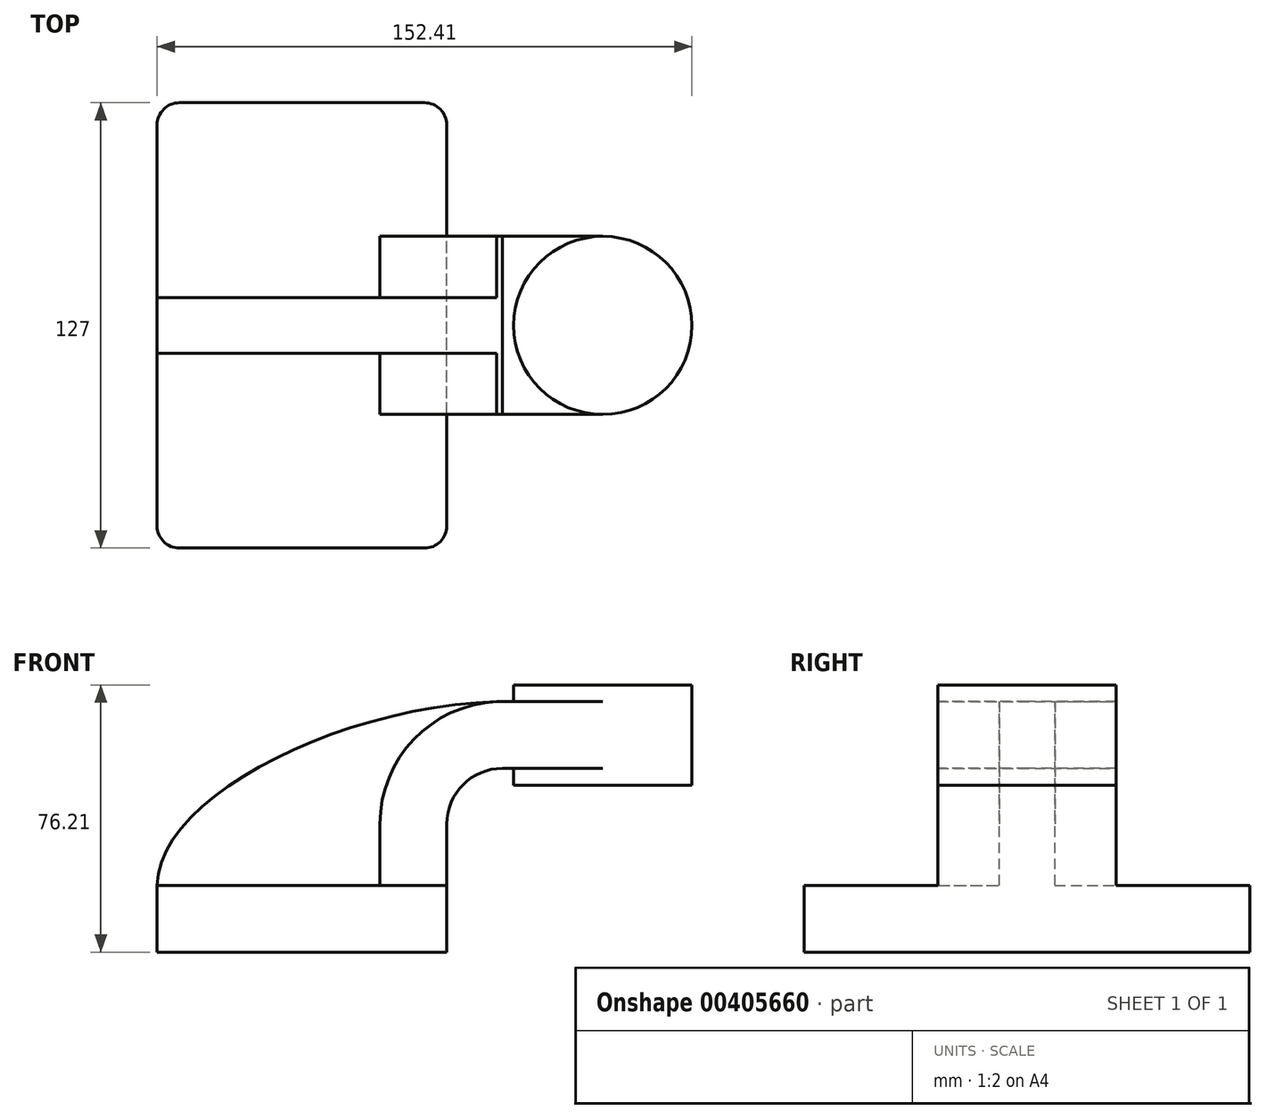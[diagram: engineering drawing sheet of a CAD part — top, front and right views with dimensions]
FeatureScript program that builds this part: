
annotation { "Feature Type Name" : "Feature", "Feature Type Description" : "" }
export const myFeature = defineFeature(function(context is Context, id is Id, definition is map)
    precondition{}
    {
        {
            var Q0;
            Q0=qCreatedBy(makeId("Front.planeOp"),FACE);
            var sketch = newSketch(context, id + "F0", { "sketchPlane" : qUnion([Q0])});
            skLineSegment(sketch, "E0.bottom", {"start": v(-41.28, -9.52) * mm, "end": v(41.28, -9.52) * mm});
            skLineSegment(sketch, "E0.top", {"start": v(-41.28, 9.52) * mm, "end": v(41.27, 9.52) * mm});
            skLineSegment(sketch, "E0.left", {"start": v(-41.27, -9.52) * mm, "end": v(-41.28, 9.52) * mm});
            skLineSegment(sketch, "E0.right", {"start": v(41.28, -9.52) * mm, "end": v(41.27, 9.52) * mm});
            skPoint(sketch, "E0.middle", {"position": v(0, 0) * mm});
            skLineSegment(sketch, "E1.bottom", {"start": v(60.32, 38.1) * mm, "end": v(111.12, 38.1) * mm});
            skLineSegment(sketch, "E1.top", {"start": v(60.32, 66.68) * mm, "end": v(111.12, 66.68) * mm});
            skLineSegment(sketch, "E1.left", {"start": v(60.32, 38.1) * mm, "end": v(60.32, 66.68) * mm});
            skLineSegment(sketch, "E1.right", {"start": v(111.12, 38.1) * mm, "end": v(111.12, 66.68) * mm});
            skPoint(sketch, "E1.middle", {"position": v(85.72, 52.39) * mm});
            skLineSegment(sketch, "E2", {"start": v(41.27, 9.52) * mm, "end": v(41.27, 27) * mm});
            skArc(sketch, "E3", {"start": v(41.27, 27) * mm, "mid": v(45.92, 38.23) * mm, "end": v(57.15, 42.88) * mm});
            skLineSegment(sketch, "E4", {"start": v(57.15, 42.88) * mm, "end": v(103.35, 42.88) * mm});
            skLineSegment(sketch, "E5.0", {"start": v(57.15, 61.93) * mm, "end": v(103.35, 61.93) * mm});
            skArc(sketch, "E5.1", {"start": v(22.22, 27) * mm, "mid": v(32.45, 51.7) * mm, "end": v(57.15, 61.93) * mm});
            skLineSegment(sketch, "E5.2", {"start": v(22.22, 9.52) * mm, "end": v(22.22, 27) * mm});
            skFitSpline(sketch, "E6", {"points": [v(-41.28, 9.53) * mm, v(57.15, 61.93) * mm], "startDerivative": vector(0.7, 76.08) * mm, "endDerivative": vector(136.98, 2.33) * mm});
            skLineSegment(sketch, "E7", {"start": v(85.72, 38.1) * mm, "end": v(85.72, 66.68) * mm});
            skSolve(sketch);
        }
        {
            var Q0;
            Q0=makeQuery(id+"F0.imprint","IMPRINT",FACE,{"disambiguationData":[TD([[makeQuery(id+"F0.imprint","IMPRINT",EDGE,{"derivedFrom":sQuery(id+"F0.wireOp",EDGE,"E0.bottom")}),1.0]])]});
            extrude(context, id + "F1", {"entities" : qUnion([Q0]), "endBound" : BoundingType.SYMMETRIC, "depth" : 127 * mm});
        }
        {
            var Q0;
            {var subQ1=sQuery(id+"F0.wireOp",EDGE,"E2");Q0=makeQuery(id+"F0.imprint","IMPRINT",FACE,{"disambiguationData":[TD([[makeQuery(id+"F0.imprint","IMPRINT",EDGE,{"derivedFrom":subQ1}),1.0]])]});}
            var Q1;
            {var subQ0=sQuery(id+"F0.wireOp",EDGE,"E4");var subQ1=sQuery(id+"F0.wireOp",EDGE,"E1.left");var subQ2=makeQuery(id+"F0.imprint","INTERSECT",VERTEX,{"derivedFrom":[subQ1,subQ0]});Q1=makeQuery(id+"F0.imprint","IMPRINT",FACE,{"disambiguationData":[TD([[makeQuery(id+"F0.imprint","IMPRINT",EDGE,{"disambiguationData":[TD([[subQ2,-1.0]])],"derivedFrom":subQ1}),-1.0]])]});}
            extrude(context, id + "F2", {"entities" : qUnion([Q0, Q1]), "operationType" : NewBodyOperationType.ADD, "endBound" : BoundingType.SYMMETRIC, "depth" : 50.8 * mm});
        }
        {
            var Q0;
            {var subQ3=sQuery(id+"F0.wireOp",EDGE,"E5.2");Q0=makeQuery(id+"F0.imprint","IMPRINT",FACE,{"disambiguationData":[TD([[makeQuery(id+"F0.imprint","IMPRINT",EDGE,{"derivedFrom":subQ3}),1.0]])]});}
            extrude(context, id + "F3", {"entities" : qUnion([Q0]), "operationType" : NewBodyOperationType.ADD, "endBound" : BoundingType.SYMMETRIC, "depth" : 15.88 * mm});
        }
        {
            var Q0;
            {var subQ4=sQuery(id+"F0.wireOp",EDGE,"E1.right");Q0=makeQuery(id+"F0.imprint","IMPRINT",FACE,{"disambiguationData":[TD([[makeQuery(id+"F0.imprint","IMPRINT",EDGE,{"derivedFrom":subQ4}),1.0]])]});}
            var Q1;
            Q1=sQuery(id+"F0.wireOp",EDGE,"E7");
            revolve(context, id + "F4", {"operationType" : NewBodyOperationType.ADD, "entities" : qUnion([Q0]), "axis" : qUnion([Q1]), "revolveType" : RevolveType.FULL});
        }
        {
            var Q0;
            Q0=makeQuery(id+"F1.opExtrude","CAP_EDGE",EDGE,{"disambiguationData":[OSD([sQuery(id+"F0.wireOp",EDGE,"E0.left")])],"isStart":false});
            var Q1;
            Q1=makeQuery(id+"F1.opExtrude","CAP_EDGE",EDGE,{"disambiguationData":[OSD([sQuery(id+"F0.wireOp",EDGE,"E0.right")])],"isStart":false});
            var Q2;
            Q2=makeQuery(id+"F1.opExtrude","CAP_EDGE",EDGE,{"disambiguationData":[OSD([sQuery(id+"F0.wireOp",EDGE,"E0.right")])],"isStart":true});
            var Q3;
            Q3=makeQuery(id+"F1.opExtrude","CAP_EDGE",EDGE,{"disambiguationData":[OSD([sQuery(id+"F0.wireOp",EDGE,"E0.left")])],"isStart":true});
            fillet(context, id + "F5", {"entities" : qUnion([Q0, Q1, Q2, Q3]), "radius" : 6.35 * mm, "tangentPropagation" : true, "allowEdgeOverflow" : false});
        }
    });
